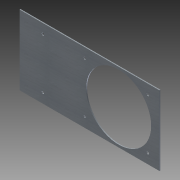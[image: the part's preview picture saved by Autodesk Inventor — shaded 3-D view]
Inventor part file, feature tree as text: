
AUTODESK INVENTOR PART (.ipt)
format: ipt  version: 2011 SP1 (Build 150282100, 282)  size: 102,400 bytes
history: native  units: in
note: dims shown in document units (in); Inventor stores cm internally (conversion verified against a paired STEP export)
features: hole x7, extrude x1, sketch x1
ambient origin geometry x8: Origin, YZ Plane, XZ Plane, XY Plane, X Axis, Y Axis, Z Axis, Center Point
bodies: Solid1 (feature_tree)
feature tree (9):
  extrude  "Extrusion1"  Depth=9.0in
  hole  "Hole1"  [1 undecoded]
  hole  "Hole2"  [1 undecoded]
  hole  "Hole3"  [1 undecoded]
  hole  "Hole4"  [1 undecoded]
  hole  "Hole5"  [1 undecoded]
  hole  "Hole6"  [1 undecoded]
  hole  "Hole7"  [1 undecoded]
  sketch  "Sketch1"  dims[d0=18.0in d1=9.0in d2=4.5in d3=5.5in d4=0.125in d5=0.0in d6=4.5in d7=5.25in d8=8.375in d9=0.75in d10=0.375in d11=0.25in d12=0.5635in d13=1.0in d14=0.8108in d15=3.0in d16=1.25in d17=0.3125in d18=0.75in d19=0.375in d20=0.25in d21=0.5635in d22=1.0in d23=0.8108in d24=1.25in d25=3.0in d26=0.3125in d27=0.75in d28=0.375in d29=0.25in d30=0.5635in d31=1.0in d32=0.8108in d33=1.25in d34=8.375in d35=0.3125in d36=0.75in d37=0.375in d38=0.25in d39=0.5635in d40=1.0in d41=0.8108in d42=1.25in d43=8.375in d44=0.25in d45=0.75in d46=0.375in d47=0.25in d48=0.5635in d49=1.0in d50=0.8108in d51=1.25in d52=16.5in d53=0.3125in d54=0.75in d55=0.375in d56=0.25in d57=0.5635in d58=1.0in d59=0.8108in d60=1.25in d61=16.5in d62=0.3125in d63=0.75in d64=0.375in d65=0.25in d66=0.5635in d67=1.0in d68=0.8108in]
note: 7 required parameter values undecoded (feature->parameter linkage not recoverable at this tier; creation-order binding heuristic only, values carry confidence <= 0.55)
